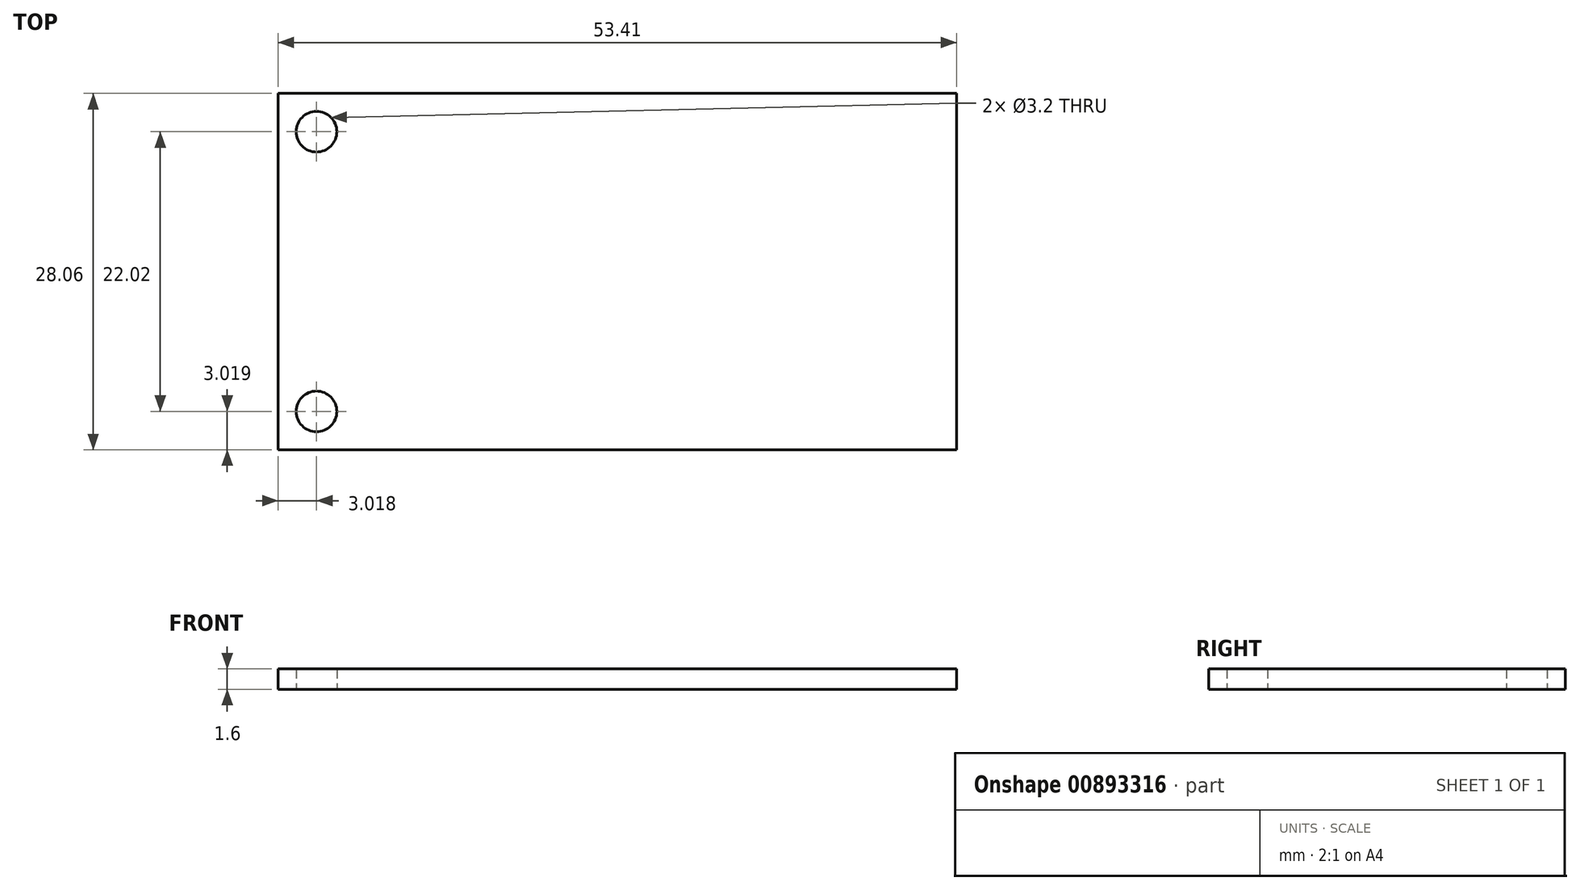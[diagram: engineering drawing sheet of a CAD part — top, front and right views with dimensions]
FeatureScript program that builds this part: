
annotation { "Feature Type Name" : "Feature", "Feature Type Description" : "" }
export const myFeature = defineFeature(function(context is Context, id is Id, definition is map)
    precondition{}
    {
        {
            var Q0;
            Q0=qCreatedBy(makeId("Top.planeOp"),FACE);
            var sketch = newSketch(context, id + "F0", { "sketchPlane" : qUnion([Q0])});
            skLineSegment(sketch, "E0.bottom", {"start": v(-21.6, -28.97) * mm, "end": v(31.82, -28.97) * mm});
            skLineSegment(sketch, "E0.top", {"start": v(-21.6, -57.03) * mm, "end": v(31.82, -57.03) * mm});
            skLineSegment(sketch, "E0.left", {"start": v(-21.6, -28.97) * mm, "end": v(-21.6, -57.03) * mm});
            skLineSegment(sketch, "E0.right", {"start": v(31.82, -28.97) * mm, "end": v(31.82, -57.03) * mm});
            skCircle(sketch, "E1", {"center": v(-18.57, -32) * mm, "radius": 1.6 * mm});
            skCircle(sketch, "E2", {"center": v(-18.57, -54.01) * mm, "radius": 1.6 * mm});
            skSolve(sketch);
        }
        {
            var Q0;
            Q0=makeQuery(id+"F0.imprint","IMPRINT",FACE,{"disambiguationData":[TD([[makeQuery(id+"F0.imprint","IMPRINT",EDGE,{"derivedFrom":sQuery(id+"F0.wireOp",EDGE,"E0.bottom")}),-1.0]])]});
            extrude(context, id + "F1", {"entities" : qUnion([Q0]), "depth" : 1.6 * mm, "offsetDistance" : 25 * mm});
        }
    });
